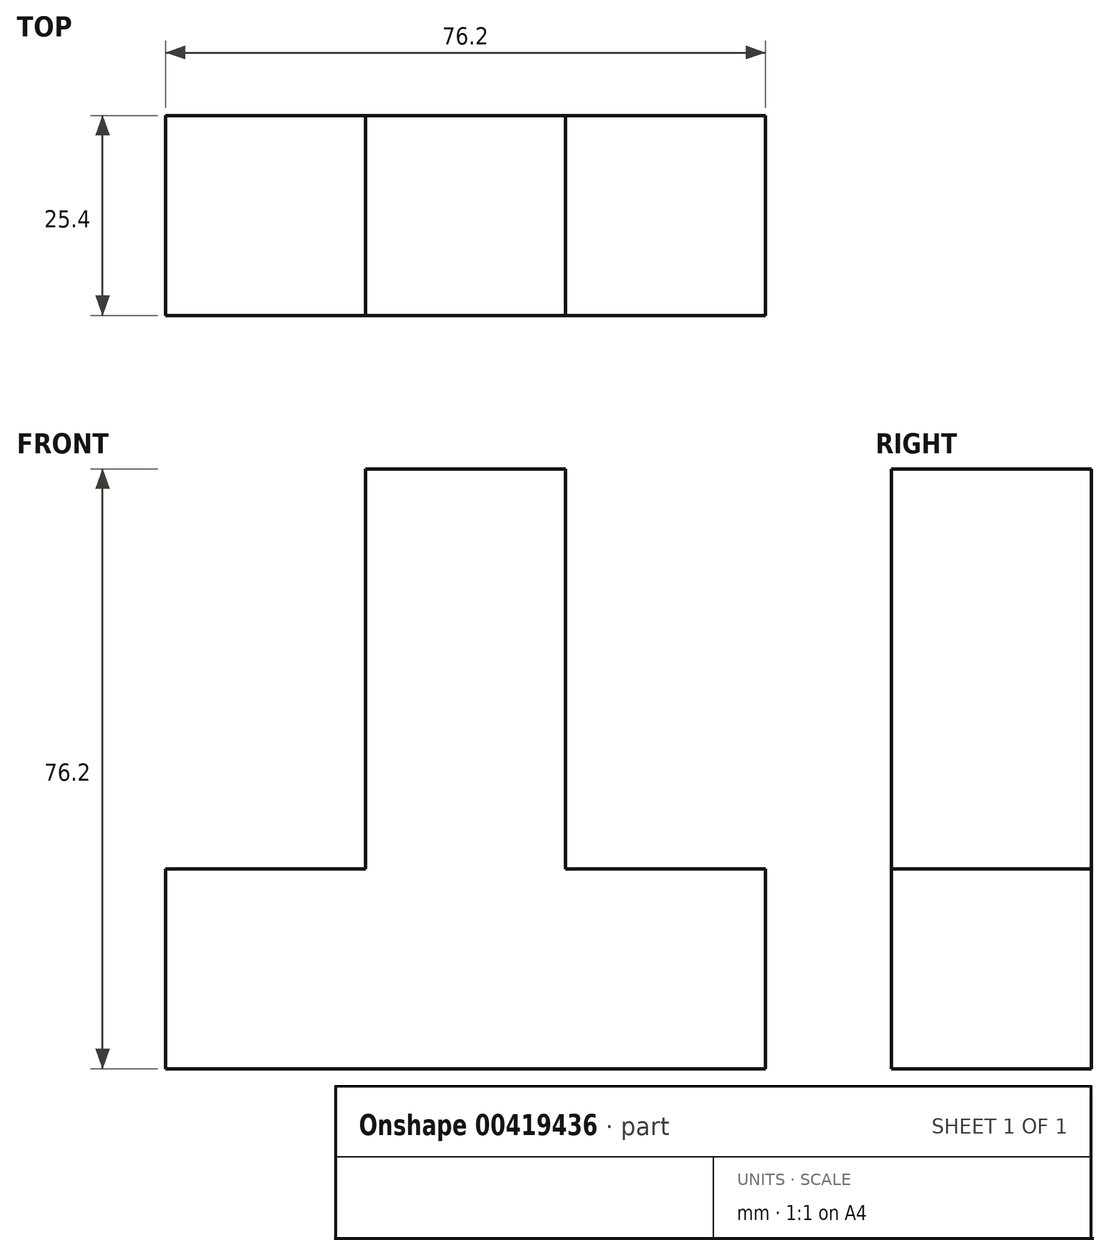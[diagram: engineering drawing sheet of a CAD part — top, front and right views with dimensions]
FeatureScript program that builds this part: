
annotation { "Feature Type Name" : "Feature", "Feature Type Description" : "" }
export const myFeature = defineFeature(function(context is Context, id is Id, definition is map)
    precondition{}
    {
        {
            var Q0;
            Q0=qCreatedBy(makeId("Front.planeOp"),FACE);
            var sketch = newSketch(context, id + "F0", { "sketchPlane" : qUnion([Q0])});
            skLineSegment(sketch, "E0", {"start": v(0, 0) * mm, "end": v(0, 25.4) * mm});
            skLineSegment(sketch, "E1", {"start": v(0, 25.4) * mm, "end": v(-25.4, 25.4) * mm});
            skLineSegment(sketch, "E2", {"start": v(-25.4, 25.4) * mm, "end": v(-25.4, 76.2) * mm});
            skLineSegment(sketch, "E3", {"start": v(-25.4, 76.2) * mm, "end": v(-50.8, 76.2) * mm});
            skLineSegment(sketch, "E4", {"start": v(-50.8, 76.2) * mm, "end": v(-50.8, 25.4) * mm});
            skLineSegment(sketch, "E5", {"start": v(-50.8, 25.4) * mm, "end": v(-76.2, 25.4) * mm});
            skLineSegment(sketch, "E6", {"start": v(-76.2, 25.4) * mm, "end": v(-76.2, 0) * mm});
            skLineSegment(sketch, "E7", {"start": v(-76.2, 0) * mm, "end": v(0, 0) * mm});
            skSolve(sketch);
        }
        {
            var Q0;
            Q0 = qSketchRegion(id + "F0", true);
            extrude(context, id + "F1", {"entities" : qUnion([Q0]), "depth" : 25.4 * mm});
        }
    });
